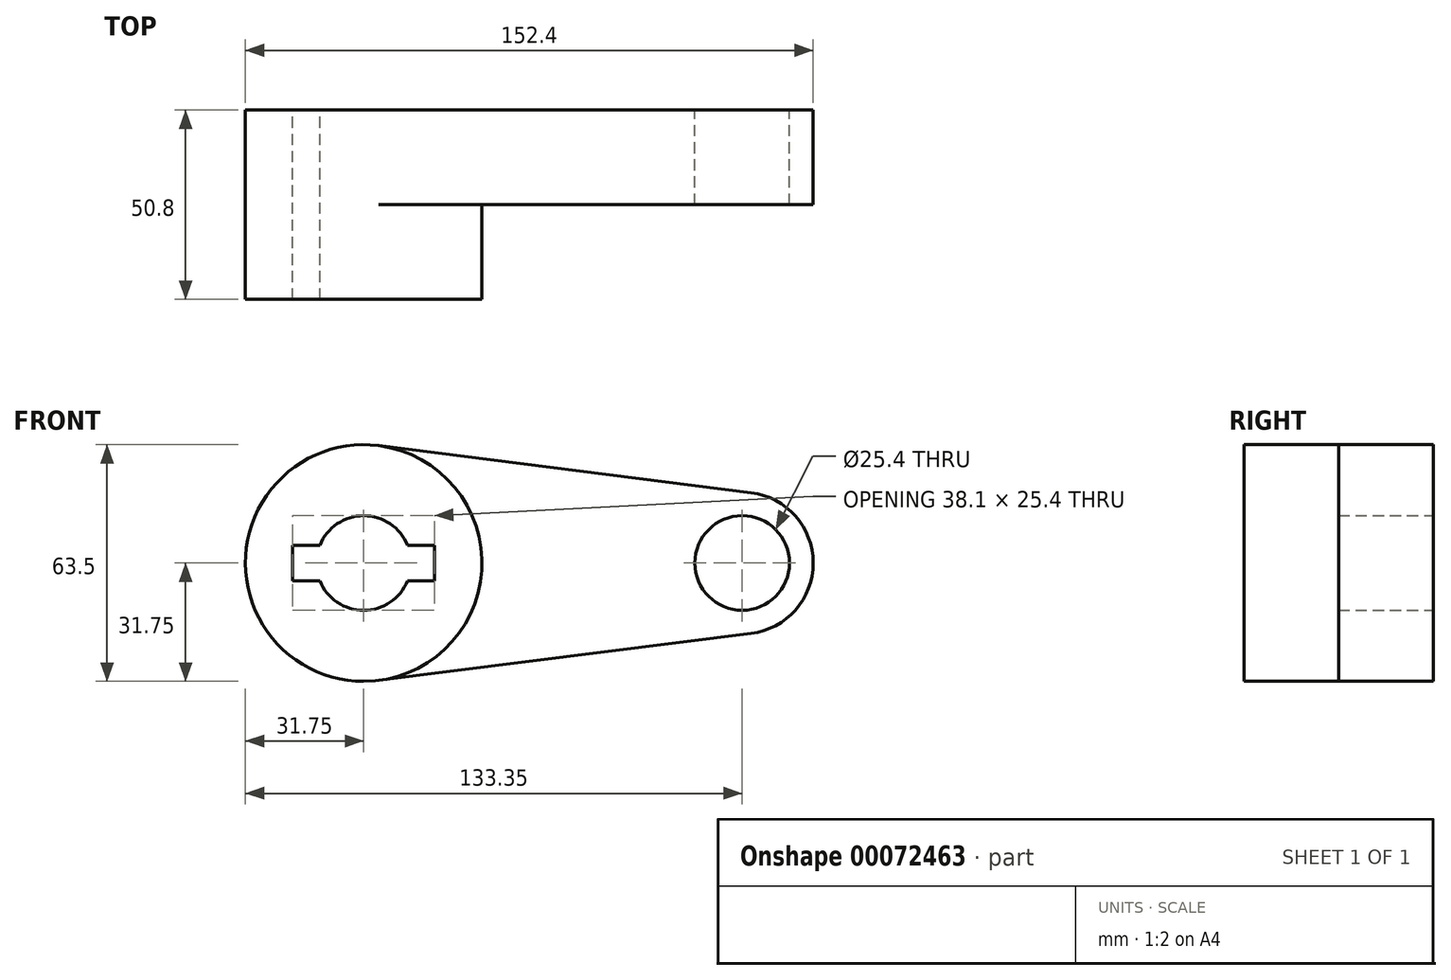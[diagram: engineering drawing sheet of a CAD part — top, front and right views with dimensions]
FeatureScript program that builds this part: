
annotation { "Feature Type Name" : "Feature", "Feature Type Description" : "" }
export const myFeature = defineFeature(function(context is Context, id is Id, definition is map)
    precondition{}
    {
        {
            var Q0;
            Q0=qCreatedBy(makeId("Front.planeOp"),FACE);
            var sketch = newSketch(context, id + "F0", { "sketchPlane" : qUnion([Q0])});
            skCircle(sketch, "E0", {"center": v(0, 0) * mm, "radius": 31.75 * mm});
            skCircle(sketch, "E1", {"center": v(101.6, 0) * mm, "radius": 19.05 * mm});
            skLineSegment(sketch, "E2", {"start": v(3.97, 31.5) * mm, "end": v(103.98, 18.9) * mm});
            skLineSegment(sketch, "E3", {"start": v(3.97, -31.5) * mm, "end": v(103.98, -18.9) * mm});
            skCircle(sketch, "E4", {"center": v(101.6, 0) * mm, "radius": 12.7 * mm});
            skCircle(sketch, "E5", {"center": v(0, 0) * mm, "radius": 12.7 * mm});
            skLineSegment(sketch, "E6.rect.bottom", {"start": v(19.05, -4.76) * mm, "end": v(-19.05, -4.76) * mm});
            skLineSegment(sketch, "E6.rect.top", {"start": v(19.05, 4.76) * mm, "end": v(-19.05, 4.76) * mm});
            skLineSegment(sketch, "E6.rect.left", {"start": v(19.05, -4.76) * mm, "end": v(19.05, 4.76) * mm});
            skLineSegment(sketch, "E6.rect.right", {"start": v(-19.05, -4.76) * mm, "end": v(-19.05, 4.76) * mm});
            skSolve(sketch);
        }
        {
            var Q0;
            Q0 = qSketchRegion(id + "F0", true);
            extrude(context, id + "F1", {"entities" : qUnion([Q0]), "depth" : 25.4 * mm});
        }
        {
            var Q0;
            {var subQ7=sQuery(id+"F0.wireOp",EDGE,"E6.rect.left");Q0=makeQuery(id+"F0.imprint","IMPRINT",FACE,{"disambiguationData":[TD([[makeQuery(id+"F0.imprint","IMPRINT",EDGE,{"derivedFrom":subQ7}),-1.0]])]});}
            extrude(context, id + "F2", {"entities" : qUnion([Q0]), "operationType" : NewBodyOperationType.ADD, "depth" : 50.8 * mm});
        }
    });
